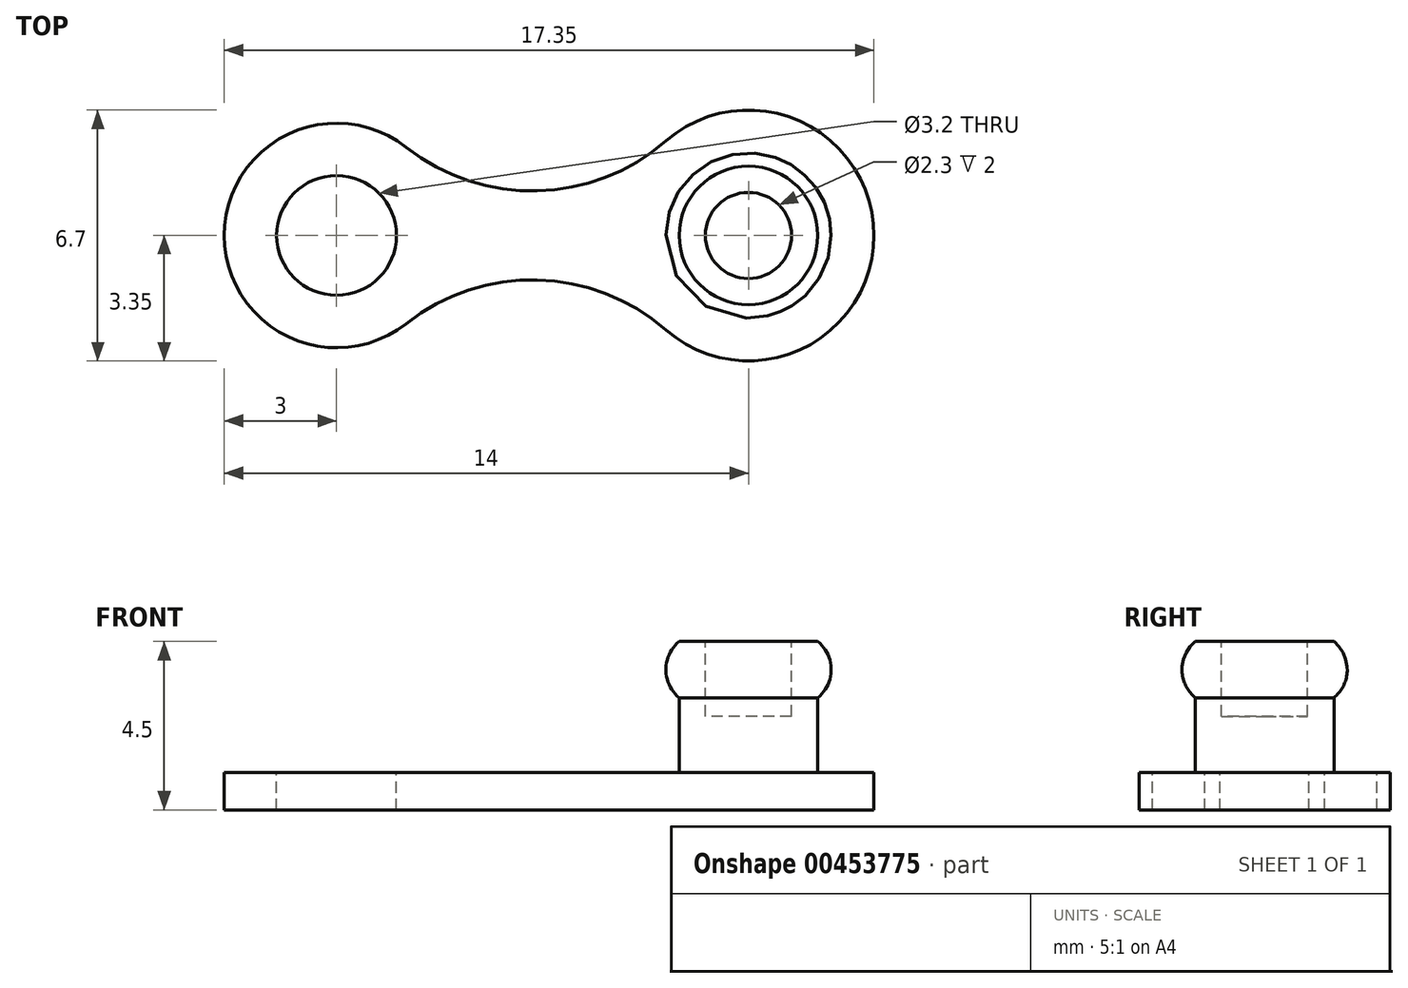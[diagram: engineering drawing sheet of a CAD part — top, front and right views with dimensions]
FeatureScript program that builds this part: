
annotation { "Feature Type Name" : "Feature", "Feature Type Description" : "" }
export const myFeature = defineFeature(function(context is Context, id is Id, definition is map)
    precondition{}
    {
        {
            var Q0;
            Q0=qCreatedBy(makeId("Top.planeOp"),FACE);
            var sketch = newSketch(context, id + "F0", { "sketchPlane" : qUnion([Q0])});
            skCircle(sketch, "E0", {"center": v(0, 0) * mm, "radius": 1.85 * mm});
            skSolve(sketch);
        }
        {
            var Q0;
            Q0=qCreatedBy(makeId("Front.planeOp"),FACE);
            var sketch = newSketch(context, id + "F1", { "sketchPlane" : qUnion([Q0])});
            skLineSegment(sketch, "E1", {"start": v(0, 1.5) * mm, "end": v(-1.85, 1.5) * mm});
            skArc(sketch, "E2", {"start": v(-1.85, 1.5) * mm, "mid": v(-2.2, 0.75) * mm, "end": v(-1.85, 0) * mm});
            skLineSegment(sketch, "E3", {"start": v(-1.85, 0) * mm, "end": v(0, 0) * mm});
            skLineSegment(sketch, "E4", {"start": v(0, 1.5) * mm, "end": v(0, 0) * mm});
            skSolve(sketch);
        }
        {
            var Q0;
            Q0=makeQuery(id+"F1.imprint","IMPRINT",FACE,{"disambiguationData":[TD([[makeQuery(id+"F1.imprint","IMPRINT",EDGE,{"derivedFrom":sQuery(id+"F1.wireOp",EDGE,"E1")}),1.0]])]});
            var Q1;
            Q1=sQuery(id+"F1.wireOp",EDGE,"E4");
            revolve(context, id + "F2", {"entities" : qUnion([Q0]), "axis" : qUnion([Q1]), "revolveType" : RevolveType.FULL});
        }
        {
            var Q0;
            Q0=makeQuery(id+"F0.imprint","IMPRINT",FACE,{"disambiguationData":[TD([[makeQuery(id+"F0.imprint","IMPRINT",EDGE,{"derivedFrom":sQuery(id+"F0.wireOp",EDGE,"E0")}),1.0]])]});
            extrude(context, id + "F3", {"entities" : qUnion([Q0]), "operationType" : NewBodyOperationType.ADD, "oppositeDirection" : true, "depth" : 2 * mm, "offsetDistance" : 25 * mm});
        }
        {
            var Q0;
            Q0=makeQuery(id+"F3.opExtrude","CAP_FACE",FACE,{"disambiguationData":[OSD([sQuery(id+"F0.wireOp",EDGE,"E0")])],"isStart":false});
            var sketch = newSketch(context, id + "F4", { "sketchPlane" : qUnion([Q0])});
            skCircle(sketch, "E5", {"center": v(0, 0) * mm, "radius": 3.35 * mm});
            skCircle(sketch, "E6", {"center": v(-11, 0) * mm, "radius": 1.6 * mm});
            skCircle(sketch, "E7", {"center": v(-11, 0) * mm, "radius": 3 * mm});
            skArc(sketch, "E8", {"start": v(-9.14, 2.36) * mm, "mid": v(-5.64, 1.19) * mm, "end": v(-2.2, 2.53) * mm});
            skLineSegment(sketch, "E9", {"start": v(-11, 0) * mm, "end": v(0, 0) * mm, "construction": true});
            skArc(sketch, "E10.MirrorCS", {"start": v(-9.14, -2.36) * mm, "mid": v(-5.64, -1.19) * mm, "end": v(-2.2, -2.53) * mm});
            skSolve(sketch);
        }
        {
            var Q0;
            {var subQ0=sQuery(id+"F4.wireOp",EDGE,"E8");Q0=makeQuery(id+"F4.imprint","IMPRINT",FACE,{"disambiguationData":[TD([[makeQuery(id+"F4.imprint","IMPRINT",EDGE,{"derivedFrom":subQ0}),-1.0]])]});}
            var Q1;
            Q1=makeQuery(id+"F4.imprint","IMPRINT",FACE,{"disambiguationData":[TD([[makeQuery(id+"F4.imprint","IMPRINT",EDGE,{"derivedFrom":makeQuery(id+"F3.opExtrude","CAP_EDGE",EDGE,{"disambiguationData":[OSD([sQuery(id+"F0.wireOp",EDGE,"E0")])],"isStart":false})}),1.0]])]});
            var Q2;
            Q2=makeQuery(id+"F4.imprint","IMPRINT",FACE,{"disambiguationData":[TD([[makeQuery(id+"F4.imprint","IMPRINT",EDGE,{"derivedFrom":sQuery(id+"F4.wireOp",EDGE,"E6")}),-1.0]])]});
            var Q3;
            Q3=makeQuery(id+"F4.imprint","IMPRINT",FACE,{"disambiguationData":[TD([[makeQuery(id+"F4.imprint","IMPRINT",EDGE,{"derivedFrom":makeQuery(id+"F3.opExtrude","CAP_EDGE",EDGE,{"disambiguationData":[OSD([sQuery(id+"F0.wireOp",EDGE,"E0")])],"isStart":false})}),-1.0]])]});
            extrude(context, id + "F5", {"entities" : qUnion([Q0, Q1, Q2, Q3]), "operationType" : NewBodyOperationType.ADD, "depth" : 1 * mm});
        }
        {
            var Q0;
            Q0=makeQuery(id+"F2.opRevolve","SWEPT_FACE",FACE,{"disambiguationData":[OSD([sQuery(id+"F1.wireOp",EDGE,"E1")])]});
            var sketch = newSketch(context, id + "F6", { "sketchPlane" : qUnion([Q0])});
            skCircle(sketch, "E11", {"center": v(0, 0) * mm, "radius": 1.15 * mm});
            skSolve(sketch);
        }
        {
            var Q0;
            Q0=qSketchRegion(id+"F6",true);
            extrude(context, id + "F7", {"entities" : qUnion([Q0]), "operationType" : NewBodyOperationType.REMOVE, "oppositeDirection" : true, "depth" : 2 * mm});
        }
    });
